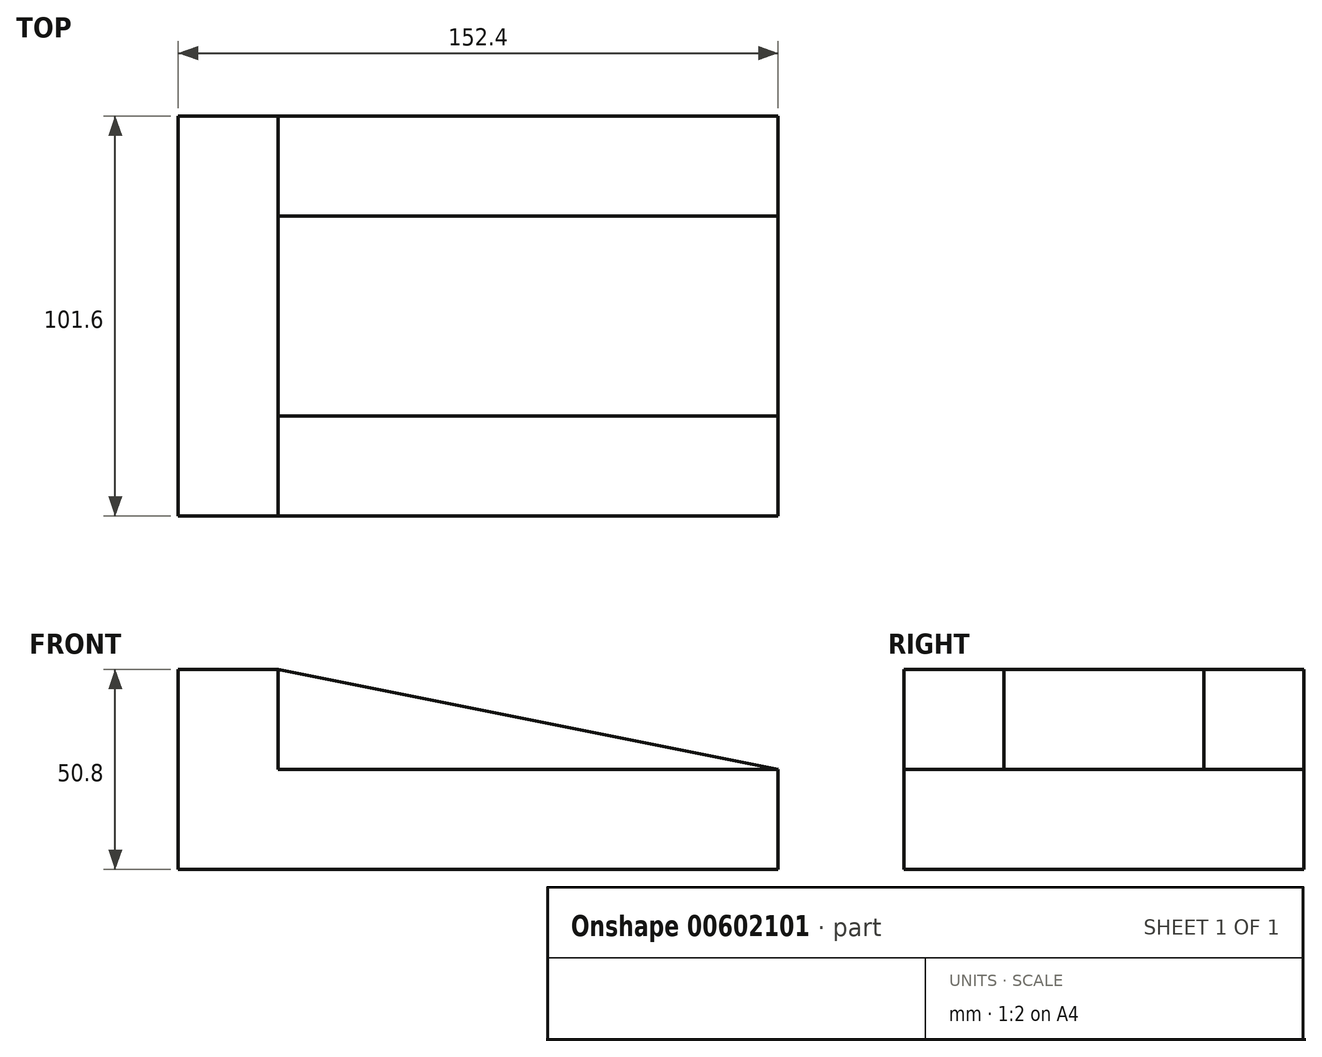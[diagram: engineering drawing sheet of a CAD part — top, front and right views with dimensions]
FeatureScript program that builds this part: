
annotation { "Feature Type Name" : "Feature", "Feature Type Description" : "" }
export const myFeature = defineFeature(function(context is Context, id is Id, definition is map)
    precondition{}
    {
        {
            var Q0;
            Q0=qCreatedBy(makeId("Front.planeOp"),FACE);
            var sketch = newSketch(context, id + "F0", { "sketchPlane" : qUnion([Q0])});
            skLineSegment(sketch, "E0.bottom", {"start": v(-80.64, -5.24) * mm, "end": v(71.76, -5.24) * mm});
            skLineSegment(sketch, "E0.top", {"start": v(-80.64, -56.04) * mm, "end": v(71.76, -56.04) * mm});
            skLineSegment(sketch, "E0.left", {"start": v(-80.64, -5.24) * mm, "end": v(-80.64, -56.04) * mm});
            skLineSegment(sketch, "E0.right", {"start": v(71.76, -5.24) * mm, "end": v(71.76, -56.04) * mm});
            skSolve(sketch);
        }
        {
            var Q0;
            Q0=makeQuery(id+"F0.imprint","IMPRINT",FACE,{"disambiguationData":[TD([[makeQuery(id+"F0.imprint","IMPRINT",EDGE,{"derivedFrom":sQuery(id+"F0.wireOp",EDGE,"E0.bottom")}),-1.0]])]});
            extrude(context, id + "F1", {"entities" : qUnion([Q0]), "oppositeDirection" : true, "depth" : 101.6 * mm, "offsetDistance" : 25.4 * mm});
        }
        {
            var Q0;
            Q0=makeQuery(id+"F1.opExtrude","SWEPT_FACE",FACE,{"disambiguationData":[OSD([sQuery(id+"F0.wireOp",EDGE,"E0.right")])]});
            var sketch = newSketch(context, id + "F2", { "sketchPlane" : qUnion([Q0])});
            skLineSegment(sketch, "E1.bottom", {"start": v(0, -5.24) * mm, "end": v(25.4, -5.24) * mm});
            skLineSegment(sketch, "E1.top", {"start": v(0, -30.64) * mm, "end": v(25.4, -30.64) * mm});
            skLineSegment(sketch, "E1.left", {"start": v(0, -5.24) * mm, "end": v(0, -30.64) * mm});
            skLineSegment(sketch, "E1.right", {"start": v(25.4, -5.24) * mm, "end": v(25.4, -30.64) * mm});
            skSolve(sketch);
        }
        {
            var Q0;
            Q0=makeQuery(id+"F2.imprint","IMPRINT",FACE,{"disambiguationData":[TD([[makeQuery(id+"F2.imprint","IMPRINT",EDGE,{"derivedFrom":sQuery(id+"F2.wireOp",EDGE,"E1.bottom")}),1.0]])]});
            extrude(context, id + "F3", {"entities" : qUnion([Q0]), "operationType" : NewBodyOperationType.REMOVE, "oppositeDirection" : true, "depth" : 127 * mm, "offsetDistance" : 25.4 * mm});
        }
        {
            var Q0;
            Q0=makeQuery(id+"F1.opExtrude","SWEPT_FACE",FACE,{"disambiguationData":[OSD([sQuery(id+"F0.wireOp",EDGE,"E0.right")])]});
            var sketch = newSketch(context, id + "F4", { "sketchPlane" : qUnion([Q0])});
            skLineSegment(sketch, "E2.bottom", {"start": v(101.6, -5.24) * mm, "end": v(76.2, -5.24) * mm});
            skLineSegment(sketch, "E2.top", {"start": v(101.6, -30.64) * mm, "end": v(76.2, -30.64) * mm});
            skLineSegment(sketch, "E2.left", {"start": v(101.6, -5.24) * mm, "end": v(101.6, -30.64) * mm});
            skLineSegment(sketch, "E2.right", {"start": v(76.2, -5.24) * mm, "end": v(76.2, -30.64) * mm});
            skSolve(sketch);
        }
        {
            var Q0;
            Q0=makeQuery(id+"F4.imprint","IMPRINT",FACE,{"disambiguationData":[TD([[makeQuery(id+"F4.imprint","IMPRINT",EDGE,{"derivedFrom":sQuery(id+"F4.wireOp",EDGE,"E2.bottom")}),1.0]])]});
            extrude(context, id + "F5", {"entities" : qUnion([Q0]), "operationType" : NewBodyOperationType.REMOVE, "oppositeDirection" : true, "depth" : 127 * mm, "offsetDistance" : 25.4 * mm});
        }
        {
            var Q0;
            Q0=makeQuery(id+"F3.boolean.opBoolean","COPY",FACE,{"derivedFrom":makeQuery(id+"F3.opExtrude","SWEPT_FACE",FACE,{"disambiguationData":[OSD([sQuery(id+"F2.wireOp",EDGE,"E1.right")])]})});
            var sketch = newSketch(context, id + "F6", { "sketchPlane" : qUnion([Q0])});
            skLineSegment(sketch, "E3", {"start": v(-55.24, -5.24) * mm, "end": v(71.76, -30.64) * mm});
            skSolve(sketch);
        }
        {
            var Q0;
            Q0=makeQuery(id+"F6.imprint","IMPRINT",FACE,{"disambiguationData":[TD([[makeQuery(id+"F6.imprint","IMPRINT",EDGE,{"derivedFrom":sQuery(id+"F6.wireOp",EDGE,"E3")}),1.0]])]});
            extrude(context, id + "F7", {"entities" : qUnion([Q0]), "operationType" : NewBodyOperationType.REMOVE, "oppositeDirection" : true, "depth" : 76.2 * mm, "offsetDistance" : 25.4 * mm});
        }
    });
